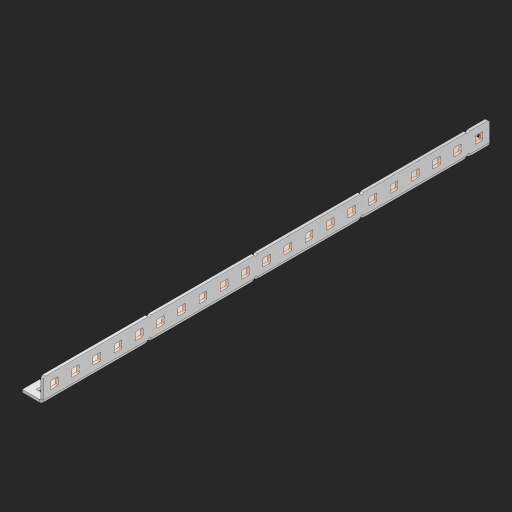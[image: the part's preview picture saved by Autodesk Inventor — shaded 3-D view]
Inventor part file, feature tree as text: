
AUTODESK INVENTOR PART (.ipt)
format: ipt  version: 2023 (Build 270158000, 158)  size: 1,018,368 bytes
history: native  units: in
note: dims shown in document units (in); Inventor stores cm internally (conversion verified against a paired STEP export)
features: other x211, extrude x61, sheet_metal_op x11, sketch x10, pattern_linear x2, mirror x1, chamfer x1
ambient origin geometry x8: Origin, YZ Plane, XZ Plane, XY Plane, X Axis, Y Axis, Z Axis, Center Point
bodies: Solid1 (feature_tree), Body (feature_tree)
feature tree (297):
  other  "Alu Half C 1x2x1x21"
  other  "Table"
  other  "Alu C 1x2x1x35"
  other  "Alu C 1x2x1x34"
  other  "Alu C 1x2x1x33"
  other  "Alu C 1x2x1x32"
  other  "Alu C 1x2x1x31"
  other  "Alu C 1x2x1x30"
  other  "Alu C 1x2x1x29"
  other  "Alu C 1x2x1x28"
  other  "Alu C 1x2x1x27"
  other  "Alu C 1x2x1x26"
  other  "Alu C 1x2x1x25"
  other  "Alu C 1x2x1x24"
  other  "Alu C 1x2x1x23"
  other  "Alu C 1x2x1x22"
  other  "Alu C 1x2x1x21"
  other  "Alu C 1x2x1x20"
  other  "Alu C 1x2x1x19"
  other  "Alu C 1x2x1x18"
  other  "Alu C 1x2x1x17"
  other  "Alu C 1x2x1x16"
  other  "Alu C 1x2x1x15"
  other  "Alu C 1x2x1x14"
  other  "Alu C 1x2x1x13"
  other  "Alu C 1x2x1x12"
  other  "Alu C 1x2x1x11"
  other  "Alu C 1x2x1x10"
  other  "Alu C 1x2x1x9"
  other  "Alu C 1x2x1x8"
  other  "Alu C 1x2x1x7"
  other  "Alu C 1x2x1x6"
  other  "Alu C 1x2x1x5"
  other  "Alu C 1x2x1x4"
  other  "Alu C 1x2x1x3"
  other  "Alu C 1x2x1x2"
  other  "Alu C 1x2x1x1"
  other  "Steel C 1x2x1x35"
  other  "Steel C 1x2x1x34"
  other  "Steel C 1x2x1x33"
  other  "Steel C 1x2x1x32"
  other  "Steel C 1x2x1x31"
  other  "Steel C 1x2x1x30"
  other  "Steel C 1x2x1x29"
  other  "Steel C 1x2x1x28"
  other  "Steel C 1x2x1x27"
  other  "Steel C 1x2x1x26"
  other  "Steel C 1x2x1x25"
  other  "Steel C 1x2x1x24"
  other  "Steel C 1x2x1x23"
  other  "Steel C 1x2x1x22"
  other  "Steel C 1x2x1x21"
  other  "Steel C 1x2x1x20"
  other  "Steel C 1x2x1x19"
  other  "Steel C 1x2x1x18"
  other  "Steel C 1x2x1x17"
  other  "Steel C 1x2x1x16"
  other  "Steel C 1x2x1x15"
  other  "Steel C 1x2x1x14"
  other  "Steel C 1x2x1x13"
  other  "Steel C 1x2x1x12"
  other  "Steel C 1x2x1x11"
  other  "Steel C 1x2x1x10"
  other  "Steel C 1x2x1x9"
  other  "Steel C 1x2x1x8"
  other  "Steel C 1x2x1x7"
  other  "Steel C 1x2x1x6"
  other  "Steel C 1x2x1x5"
  other  "Steel C 1x2x1x4"
  other  "Steel C 1x2x1x3"
  other  "Steel C 1x2x1x2"
  other  "Steel C 1x2x1x1"
  other  "Alu Half C 1x2x1x35"
  other  "Alu Half C 1x2x1x34"
  other  "Alu Half C 1x2x1x33"
  other  "Alu Half C 1x2x1x32"
  other  "Alu Half C 1x2x1x31"
  other  "Alu Half C 1x2x1x30"
  other  "Alu Half C 1x2x1x29"
  other  "Alu Half C 1x2x1x28"
  other  "Alu Half C 1x2x1x27"
  other  "Alu Half C 1x2x1x26"
  other  "Alu Half C 1x2x1x25"
  other  "Alu Half C 1x2x1x24"
  other  "Alu Half C 1x2x1x23"
  other  "Alu Half C 1x2x1x22"
  other  "Alu Half C 1x2x1x20"
  other  "Alu Half C 1x2x1x19"
  other  "Alu Half C 1x2x1x18"
  other  "Alu Half C 1x2x1x17"
  other  "Alu Half C 1x2x1x16"
  other  "Alu Half C 1x2x1x15"
  other  "Alu Half C 1x2x1x14"
  other  "Alu Half C 1x2x1x13"
  other  "Alu Half C 1x2x1x12"
  other  "Alu Half C 1x2x1x11"
  other  "Alu Half C 1x2x1x10"
  other  "Alu Half C 1x2x1x9"
  other  "Alu Half C 1x2x1x8"
  other  "Alu Half C 1x2x1x7"
  other  "Alu Half C 1x2x1x6"
  other  "Alu Half C 1x2x1x5"
  other  "Alu Half C 1x2x1x4"
  other  "Alu Half C 1x2x1x3"
  other  "Alu Half C 1x2x1x2"
  other  "Alu Half C 1x2x1x1"
  other  "Steel Half C 1x2x1x35"
  other  "Steel Half C 1x2x1x34"
  other  "Steel Half C 1x2x1x33"
  other  "Steel Half C 1x2x1x32"
  other  "Steel Half C 1x2x1x31"
  other  "Steel Half C 1x2x1x30"
  other  "Steel Half C 1x2x1x29"
  other  "Steel Half C 1x2x1x28"
  other  "Steel Half C 1x2x1x27"
  other  "Steel Half C 1x2x1x26"
  other  "Steel Half C 1x2x1x25"
  other  "Steel Half C 1x2x1x24"
  other  "Steel Half C 1x2x1x23"
  other  "Steel Half C 1x2x1x22"
  other  "Steel Half C 1x2x1x21"
  other  "Steel Half C 1x2x1x20"
  other  "Steel Half C 1x2x1x19"
  other  "Steel Half C 1x2x1x18"
  other  "Steel Half C 1x2x1x17"
  other  "Steel Half C 1x2x1x16"
  other  "Steel Half C 1x2x1x15"
  other  "Steel Half C 1x2x1x14"
  other  "Steel Half C 1x2x1x13"
  other  "Steel Half C 1x2x1x12"
  other  "Steel Half C 1x2x1x11"
  other  "Steel Half C 1x2x1x10"
  other  "Steel Half C 1x2x1x9"
  other  "Steel Half C 1x2x1x8"
  other  "Steel Half C 1x2x1x7"
  other  "Steel Half C 1x2x1x6"
  other  "Steel Half C 1x2x1x5"
  other  "Steel Half C 1x2x1x4"
  other  "Steel Half C 1x2x1x3"
  other  "Steel Half C 1x2x1x2"
  other  "Steel Half C 1x2x1x1"
  sheet_metal_op  "Flanges"
  other  "Flange Pattern Plane"
  other  "Flange Pattern Sketch"
  sheet_metal_op  "Flange Pattern"
  sheet_metal_op  "Body Pattern"
  pattern_linear  "Center Pattern"  Spacing1=0.0625in  [1 undecoded]
  other  "Arc Length"
  mirror  "Notch Mirror"
  pattern_linear  "Notch Pattern"  Spacing1=0.182in  [1 undecoded]
  chamfer  "End Chamfer"
  extrude  "Half Cut"  Depth=0.02in
  sketch  "Sketch1"  dims[d0=1.0in]
  other  "Plate1"
  sketch  "Sketch2"  dims[d1=10.5in]
  other  "Plate2"
  sheet_metal_op  "Bend1"
  sheet_metal_op  "Corner1"
  sketch  "Sketch3"  dims[d2=0.0625in]
  sketch  "Sketch7"  dims[d3=0.0625in]
  other  "Srf1"
  other  "Srf2"
  sketch  "Sketch8"  dims[d4=0.0312in]
  sketch  "Sketch9"  dims[d5=0.125in]
  other  "Srf91"
  sheet_metal_op  "Body Pattern Sketch"
  other  "Srf92"
  sketch  "Sketch13"  dims[d6=0.0625in]
  sketch  "Sketch14"  dims[d7=0.5in d8=90.0deg d9=0.0312in]
  sketch  "Sketch15"  dims[d10=0.25in]
  sketch  "Sketch16"  dims[d11=0.0625in d12=0.0625in d16=0.182in d17=0.02in d18=0.0625in d19=0.0in d20=0.25in d21=0.25in d38=8.2677in d40=0.5in d41=0.3937in d43=1.0in d46=0.172in d47=1.0in d48=0.0in d49=0.182in d50=0.02in d51=0.25in d52=0.25in d53=0.0625in d54=0.0in d55=0.172in d56=1.0in d57=0.0in d58=0.25in d60=8.2677in d62=0.5in d63=0.3937in d65=0.5in d85=0.1473in d86=0.1782in d88=0.04in d89=0.0625in d90=0.0in d91=0.04in d92=0.0491in d95=2.5in d96=0.04in d97=0.25in d98=45.0deg d99=0.25in d100=0.5in d101=0.0in d102=2.497in d106=0.182in d107=0.02in d108=0.5in d109=0.5in d110=0.0625in d111=0.0in d112=0.172in d113=0.5in d114=0.0in d117=0.5in d118=0.5in d119=0.5in]
  other  "Srf786"
  other  "Srf823"
  other  "Srf824"
  other  "Srf825"
  other  "Srf826"
  other  "Srf827"
  other  "Srf828"
  other  "Srf829"
  other  "Srf856"
  other  "Srf857"
  other  "Srf858"
  other  "Srf859"
  other  "Srf860"
  other  "Srf861"
  other  "Srf862"
  other  "Srf889"
  other  "Srf890"
  other  "Srf891"
  other  "Srf892"
  other  "Srf893"
  other  "Srf894"
  other  "Srf895"
  other  "Srf896"
  other  "Srf922"
  other  "Srf923"
  other  "Srf924"
  other  "Srf925"
  other  "Srf926"
  other  "Srf959"
  other  "Srf960"
  other  "Srf961"
  other  "Srf962"
  other  "Srf963"
  other  "Srf996"
  other  "Srf997"
  other  "Srf998"
  other  "Srf999"
  other  "Srf1000"
  other  "Srf1143"
  other  "Srf1144"
  other  "Srf1145"
  other  "Srf1146"
  other  "Srf1147"
  other  "Srf1148"
  other  "Srf1149"
  other  "Srf1199"
  other  "Srf1200"
  other  "Srf1201"
  other  "Srf1202"
  other  "Srf1203"
  other  "Srf1204"
  other  "Srf1205"
  other  "Srf1255"
  other  "Srf1256"
  other  "Srf1257"
  other  "Srf1258"
  other  "Srf1259"
  other  "Srf1260"
  other  "Srf1261"
  sheet_metal_op  "Flange Stamp"
  sheet_metal_op  "Flange Circle"
  sheet_metal_op  "Body Stamp"
  sheet_metal_op  "Body Circle"
  other  "Center Stamp"
  other  "Center Circle"
  sheet_metal_op  "Notch"
  extrude  "ExtrusionSrf2"  Depth=0.0625in
  extrude  "ExtrusionSrf92"  TaperAngle=0.0deg  [1 undecoded]
  extrude  "ExtrusionSrf823"  Depth=0.5in
  extrude  "ExtrusionSrf824"  Depth=0.5in
  extrude  "ExtrusionSrf825"  Depth=0.5in
  extrude  "ExtrusionSrf826"  Depth=0.5in
  extrude  "ExtrusionSrf827"  Depth=1.0in TaperAngle=0.0deg
  extrude  "ExtrusionSrf828"  Depth=0.182in
  extrude  "ExtrusionSrf829"  Depth=0.02in
  extrude  "ExtrusionSrf856"  Depth=0.5in
  extrude  "ExtrusionSrf857"  Depth=0.5in
  extrude  "ExtrusionSrf858"  Depth=0.0625in
  extrude  "ExtrusionSrf859"  TaperAngle=0.0deg  [1 undecoded]
  extrude  "ExtrusionSrf860"  Depth=0.5in
  extrude  "ExtrusionSrf861"  Depth=1.0in TaperAngle=0.0deg
  extrude  "ExtrusionSrf862"  Depth=0.5in
  extrude  "ExtrusionSrf889"  Depth=0.5in
  extrude  "ExtrusionSrf890"  Depth=0.5in
  extrude  "ExtrusionSrf891"  Depth=0.5in
  extrude  "ExtrusionSrf892"  Depth=0.5in
  extrude  "ExtrusionSrf893"  Depth=0.5in
  extrude  "ExtrusionSrf894"  Depth=0.0625in
  extrude  "ExtrusionSrf895"  TaperAngle=0.0deg  [1 undecoded]
  extrude  "ExtrusionSrf896"  Depth=0.5in
  extrude  "ExtrusionSrf922"  Depth=0.5in
  extrude  "ExtrusionSrf923"  Depth=0.5in
  extrude  "ExtrusionSrf924"  Depth=0.5in TaperAngle=45.0deg
  extrude  "ExtrusionSrf925"  Depth=0.5in
  extrude  "ExtrusionSrf926"  Depth=0.5in TaperAngle=0.0deg
  extrude  "ExtrusionSrf959"  Depth=0.5in
  extrude  "ExtrusionSrf960"  Depth=0.182in
  extrude  "ExtrusionSrf961"  Depth=0.02in
  extrude  "ExtrusionSrf962"  Depth=0.5in
  extrude  "ExtrusionSrf963"  Depth=0.5in
  extrude  "ExtrusionSrf996"  Depth=0.0625in
  extrude  "ExtrusionSrf997"  TaperAngle=0.0deg  [1 undecoded]
  extrude  "ExtrusionSrf998"  Depth=0.5in
  extrude  "ExtrusionSrf999"  Depth=0.5in TaperAngle=0.0deg
  extrude  "ExtrusionSrf1000"  Depth=0.5in
  extrude  "ExtrusionSrf1143"  Depth=0.5in
  extrude  "ExtrusionSrf1144"  Depth=0.5in
  extrude  "ExtrusionSrf1145"  [1 undecoded]
  extrude  "ExtrusionSrf1146"  [1 undecoded]
  extrude  "ExtrusionSrf1147"  [1 undecoded]
  extrude  "ExtrusionSrf1148"  [1 undecoded]
  extrude  "ExtrusionSrf1149"  [1 undecoded]
  extrude  "ExtrusionSrf1199"  [1 undecoded]
  extrude  "ExtrusionSrf1200"  [1 undecoded]
  extrude  "ExtrusionSrf1201"  [1 undecoded]
  extrude  "ExtrusionSrf1202"  [1 undecoded]
  extrude  "ExtrusionSrf1203"  [1 undecoded]
  extrude  "ExtrusionSrf1204"  [1 undecoded]
  extrude  "ExtrusionSrf1205"  [1 undecoded]
  extrude  "ExtrusionSrf1255"  [1 undecoded]
  extrude  "ExtrusionSrf1256"  [1 undecoded]
  extrude  "ExtrusionSrf1257"  [1 undecoded]
  extrude  "ExtrusionSrf1258"  [1 undecoded]
  extrude  "ExtrusionSrf1259"  [1 undecoded]
  extrude  "ExtrusionSrf1260"  [1 undecoded]
  extrude  "ExtrusionSrf1261"  [1 undecoded]
note: 25 required parameter values undecoded (feature->parameter linkage not recoverable at this tier; creation-order binding heuristic only, values carry confidence <= 0.55)
